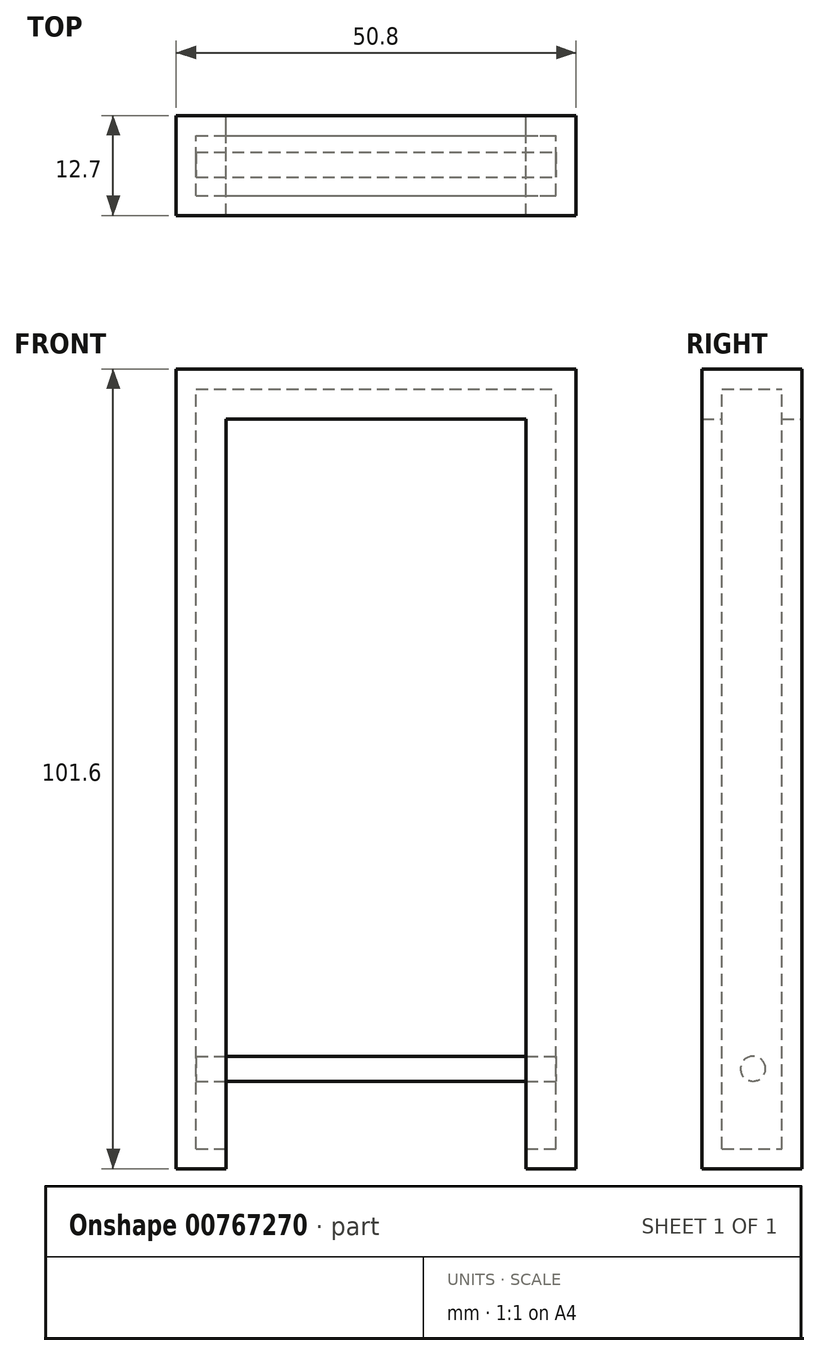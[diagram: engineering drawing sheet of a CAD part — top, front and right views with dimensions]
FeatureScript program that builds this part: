
annotation { "Feature Type Name" : "Feature", "Feature Type Description" : "" }
export const myFeature = defineFeature(function(context is Context, id is Id, definition is map)
    precondition{}
    {
        {
            var Q0;
            Q0=qCreatedBy(makeId("Front.planeOp"),FACE);
            var sketch = newSketch(context, id + "F0", { "sketchPlane" : qUnion([Q0])});
            skLineSegment(sketch, "E0.bottom", {"start": v(-105.32, -12.7) * mm, "end": v(-54.52, -12.7) * mm});
            skLineSegment(sketch, "E0.top", {"start": v(-105.32, 88.9) * mm, "end": v(-54.52, 88.9) * mm});
            skLineSegment(sketch, "E0.left", {"start": v(-105.32, -12.7) * mm, "end": v(-105.32, 88.9) * mm});
            skLineSegment(sketch, "E0.right", {"start": v(-54.52, -12.7) * mm, "end": v(-54.52, 88.9) * mm});
            skLineSegment(sketch, "E1.top", {"start": v(-98.97, 82.55) * mm, "end": v(-60.87, 82.55) * mm});
            skLineSegment(sketch, "E1.left", {"start": v(-98.97, 0) * mm, "end": v(-98.97, 82.55) * mm});
            skLineSegment(sketch, "E1.right", {"start": v(-60.87, 0) * mm, "end": v(-60.87, 82.55) * mm});
            skLineSegment(sketch, "E2", {"start": v(-98.97, 0) * mm, "end": v(-98.97, -12.7) * mm});
            skLineSegment(sketch, "E3", {"start": v(-60.87, 0) * mm, "end": v(-60.87, -12.7) * mm});
            skLineSegment(sketch, "E4", {"start": v(-60.87, -12.7) * mm, "end": v(-98.97, -12.7) * mm});
            skSolve(sketch);
        }
        {
            var Q0;
            Q0=makeQuery(id+"F0.imprint","IMPRINT",FACE,{"disambiguationData":[TD([[makeQuery(id+"F0.imprint","IMPRINT",EDGE,{"derivedFrom":sQuery(id+"F0.wireOp",EDGE,"E0.bottom")}),1.0]])]});
            extrude(context, id + "F1", {"entities" : qUnion([Q0]), "depth" : 12.7 * mm, "offsetDistance" : 25.4 * mm});
        }
        {
            var Q0;
            Q0=makeQuery(id+"F1.opExtrude","SWEPT_FACE",FACE,{"disambiguationData":[OSD([sQuery(id+"F0.wireOp",EDGE,"E1.bottom")])]});
            var Q1;
            Q1=makeQuery(id+"F1.opExtrude","SWEPT_FACE",FACE,{"disambiguationData":[OSD([sQuery(id+"F0.wireOp",EDGE,"E1.right")])]});
            var Q2;
            Q2=makeQuery(id+"F1.opExtrude","SWEPT_FACE",FACE,{"disambiguationData":[OSD([sQuery(id+"F0.wireOp",EDGE,"E1.top")])]});
            var Q3;
            Q3=makeQuery(id+"F1.opExtrude","SWEPT_FACE",FACE,{"disambiguationData":[OSD([sQuery(id+"F0.wireOp",EDGE,"E1.left")])]});
            shell(context, id + "F2", {"entities" : qUnion([Q0, Q1, Q2, Q3]), "thickness" : 2.54 * mm});
        }
        {
            var Q0;
            Q0=makeQuery(id+"F2.opShell","OFFSET_FACE",FACE,{"disambiguationData":[OSD([sQuery(id+"F0.wireOp",EDGE,"E0.right")])]});
            var sketch = newSketch(context, id + "F3", { "sketchPlane" : qUnion([Q0])});
            skCircle(sketch, "E5", {"center": v(6.23, 0) * mm, "radius": 1.59 * mm});
            skSolve(sketch);
        }
        {
            var Q0;
            Q0=qSketchRegion(id+"F3",true);
            extrude(context, id + "F4", {"entities" : qUnion([Q0]), "operationType" : NewBodyOperationType.ADD, "depth" : 45.72 * mm, "offsetDistance" : 25.4 * mm});
        }
    });
